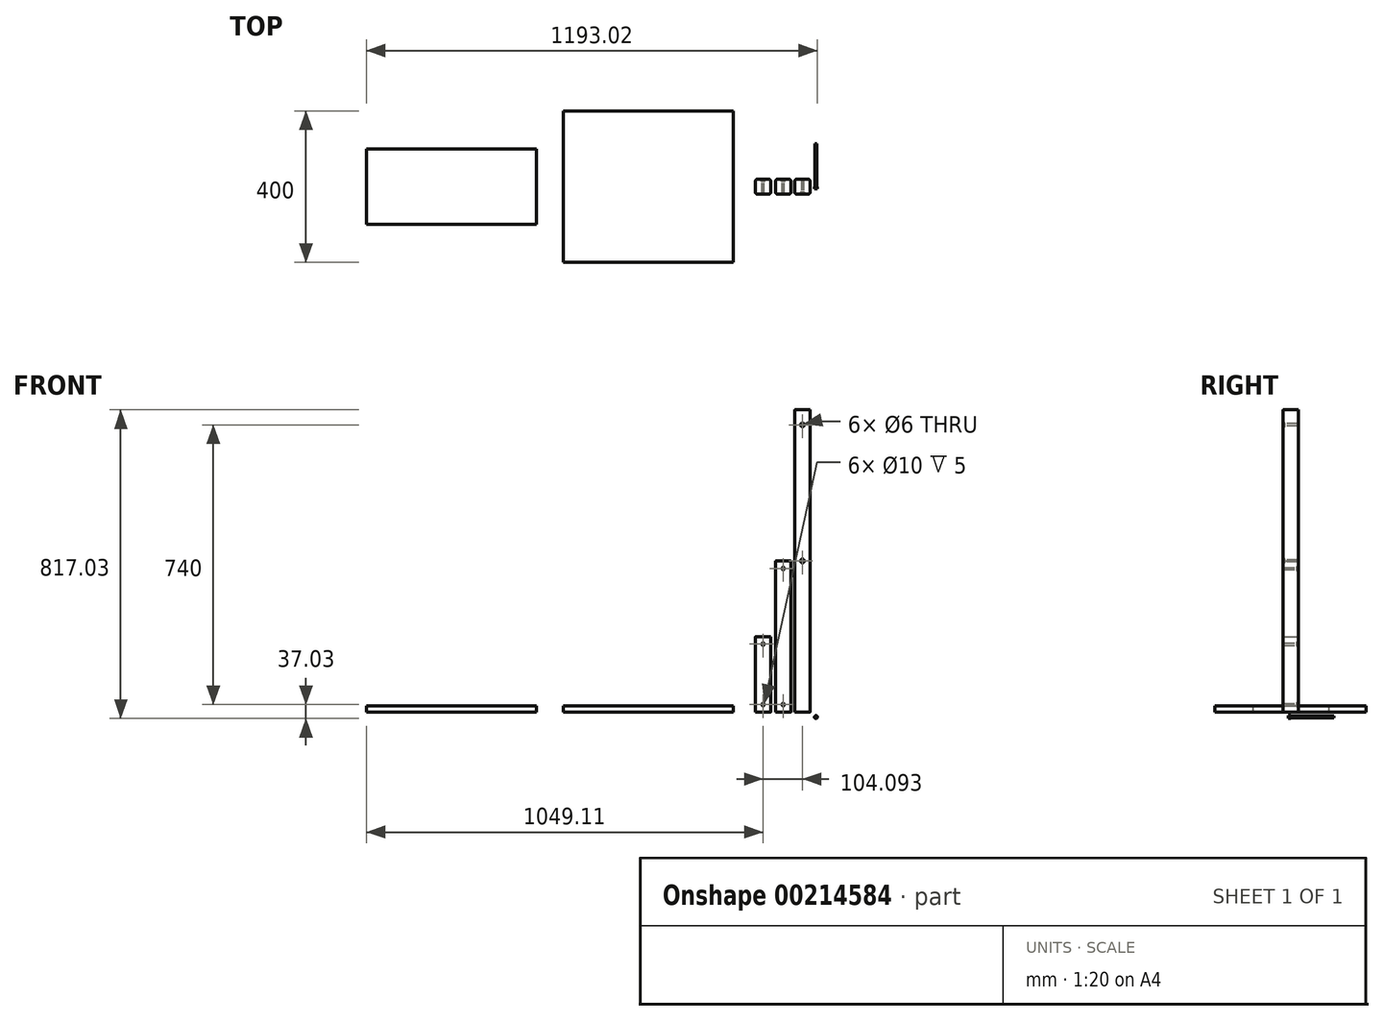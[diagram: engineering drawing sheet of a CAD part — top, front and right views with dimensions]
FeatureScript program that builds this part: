
annotation { "Feature Type Name" : "Feature", "Feature Type Description" : "" }
export const myFeature = defineFeature(function(context is Context, id is Id, definition is map)
    precondition{}
    {
        {
            var Q0;
            Q0=qCreatedBy(makeId("Top.planeOp"),FACE);
            var sketch = newSketch(context, id + "F0", { "sketchPlane" : qUnion([Q0])});
            skLineSegment(sketch, "E0.bottom", {"start": v(20, -20) * mm, "end": v(-20, -20) * mm});
            skLineSegment(sketch, "E0.top", {"start": v(20, 20) * mm, "end": v(-20, 20) * mm});
            skLineSegment(sketch, "E0.left", {"start": v(20, -20) * mm, "end": v(20, 20) * mm});
            skLineSegment(sketch, "E0.right", {"start": v(-20, -20) * mm, "end": v(-20, 20) * mm});
            skPoint(sketch, "E0.middle", {"position": v(0, 0) * mm});
            skSolve(sketch);
        }
        {
            var Q0;
            Q0 = qSketchRegion(id + "F0", true);
            extrude(context, id + "F1", {"entities" : qUnion([Q0]), "depth" : 800 * mm});
        }
        {
            var Q0;
            Q0=makeQuery(id+"F1.opExtrude","SWEPT_FACE",FACE,{"disambiguationData":[OSD([sQuery(id+"F0.wireOp",EDGE,"E0.bottom")])]});
            var sketch = newSketch(context, id + "F2", { "sketchPlane" : qUnion([Q0])});
            skPoint(sketch, "E1", {"position": v(0, 400) * mm});
            skPoint(sketch, "E2", {"position": v(0, 760) * mm});
            skSolve(sketch);
        }
        {
            var Q0;
            Q0=sQuery(id+"F2.wireOp",VERTEX,"E2");
            var Q1;
            Q1=sQuery(id+"F2.wireOp",VERTEX,"E1");
            var Q2;
            Q2=makeQuery(id+"F1.opExtrude","SWEPT_BODY",BODY,{"disambiguationData":[OSD([sQuery(id+"F0.wireOp",EDGE,"E0.bottom"),sQuery(id+"F0.wireOp",EDGE,"E0.top"),sQuery(id+"F0.wireOp",EDGE,"E0.left"),sQuery(id+"F0.wireOp",EDGE,"E0.right")])]});
            hole(context, id + "F3", {"style" : HoleStyle.C_BORE, "endStyle" : HoleEndStyle.THROUGH, "holeDiameter" : 6 * mm, "cBoreDiameter" : 10 * mm, "cBoreDepth" : 5 * mm, "locations" : qUnion([Q0, Q1]), "scope" : qUnion([Q2]), "isTappedThrough" : true});
        }
        {
            var Q0;
            Q0=makeQuery(id+"F1.opExtrude","SWEPT_EDGE",EDGE,{"disambiguationData":[OSD([sQuery(id+"F0.wireOp",EDGE,"E0.top"),sQuery(id+"F0.wireOp",EDGE,"E0.right")])]});
            var Q1;
            Q1=makeQuery(id+"F1.opExtrude","SWEPT_EDGE",EDGE,{"disambiguationData":[OSD([sQuery(id+"F0.wireOp",EDGE,"E0.top"),sQuery(id+"F0.wireOp",EDGE,"E0.left")])]});
            var Q2;
            Q2=makeQuery(id+"F1.opExtrude","SWEPT_EDGE",EDGE,{"disambiguationData":[OSD([sQuery(id+"F0.wireOp",EDGE,"E0.bottom"),sQuery(id+"F0.wireOp",EDGE,"E0.right")])]});
            var Q3;
            Q3=makeQuery(id+"F1.opExtrude","SWEPT_EDGE",EDGE,{"disambiguationData":[OSD([sQuery(id+"F0.wireOp",EDGE,"E0.bottom"),sQuery(id+"F0.wireOp",EDGE,"E0.left")])]});
            fillet(context, id + "F4", {"entities" : qUnion([Q0, Q1, Q2, Q3]), "radius" : 5 * mm, "tangentPropagation" : true, "allowEdgeOverflow" : false});
        }
        {
            var Q0;
            Q0=qCreatedBy(makeId("Front.planeOp"),FACE);
            var sketch = newSketch(context, id + "F5", { "sketchPlane" : qUnion([Q0])});
            skCircle(sketch, "E3", {"center": v(35.82, -13.03) * mm, "radius": 4 * mm});
            skSolve(sketch);
        }
        {
            var Q0;
            Q0 = qSketchRegion(id + "F5", true);
            extrude(context, id + "F6", {"entities" : qUnion([Q0]), "depth" : 6 * mm});
        }
        {
            var Q0;
            Q0=makeQuery(id+"F6.opExtrude","CAP_FACE",FACE,{"disambiguationData":[OSD([sQuery(id+"F5.wireOp",EDGE,"E3")])],"isStart":false});
            var sketch = newSketch(context, id + "F7", { "sketchPlane" : qUnion([Q0])});
            skCircle(sketch, "E4", {"center": v(35.82, -13.03) * mm, "radius": 2.5 * mm});
            skSolve(sketch);
        }
        {
            var Q0;
            Q0 = qSketchRegion(id + "F7", true);
            extrude(context, id + "F8", {"entities" : qUnion([Q0]), "operationType" : NewBodyOperationType.ADD, "oppositeDirection" : true, "depth" : 120 * mm});
        }
        {
            var Q0;
            Q0=makeQuery(id+"F6.opExtrude","CAP_FACE",FACE,{"disambiguationData":[OSD([sQuery(id+"F5.wireOp",EDGE,"E3")])],"isStart":false});
            var sketch = newSketch(context, id + "F9", { "sketchPlane" : qUnion([Q0])});
            skCircle(sketch, "E5", {"center": v(35.82, -13.03) * mm, "radius": 2.5 * mm});
            skCircle(sketch, "E6.cCircle", {"center": v(35.82, -13.03) * mm, "radius": 2.5 * mm, "construction": true});
            skLineSegment(sketch, "E6.0", {"start": v(36.75, -10.3) * mm, "end": v(38.66, -12.46) * mm});
            skLineSegment(sketch, "E6.1", {"start": v(38.66, -12.46) * mm, "end": v(37.73, -15.2) * mm});
            skLineSegment(sketch, "E6.2", {"start": v(37.73, -15.2) * mm, "end": v(34.9, -15.76) * mm});
            skLineSegment(sketch, "E6.3", {"start": v(34.9, -15.76) * mm, "end": v(33, -13.59) * mm});
            skLineSegment(sketch, "E6.4", {"start": v(33, -13.59) * mm, "end": v(33.92, -10.85) * mm});
            skLineSegment(sketch, "E6.5", {"start": v(33.92, -10.85) * mm, "end": v(36.75, -10.3) * mm});
            skPoint(sketch, "E6.0.midPoint", {"position": v(37.7, -11.38) * mm});
            skSolve(sketch);
        }
        {
            var Q0;
            Q0 = qSketchRegion(id + "F9", true);
            var Q1;
            Q1=sQuery(id+"F9.wireOp",EDGE,"E6.0");
            var Q2;
            Q2=sQuery(id+"F9.wireOp",EDGE,"E6.5");
            var Q3;
            Q3=sQuery(id+"F9.wireOp",EDGE,"E6.4");
            var Q4;
            Q4=sQuery(id+"F9.wireOp",EDGE,"E6.3");
            var Q5;
            Q5=sQuery(id+"F9.wireOp",EDGE,"E6.1");
            var Q6;
            Q6=sQuery(id+"F9.wireOp",EDGE,"E6.2");
            extrude(context, id + "F10", {"entities" : qUnion([Q0]), "operationType" : NewBodyOperationType.REMOVE, "surfaceEntities" : qUnion([Q1, Q2, Q3, Q4, Q5, Q6]), "oppositeDirection" : true, "depth" : 4 * mm});
        }
        {
            var Q0;
            Q0=qCreatedBy(makeId("Top.planeOp"),FACE);
            var sketch = newSketch(context, id + "F11", { "sketchPlane" : qUnion([Q0])});
            skLineSegment(sketch, "E7.bottom", {"start": v(-30.83, -20) * mm, "end": v(-70.83, -20) * mm});
            skLineSegment(sketch, "E7.top", {"start": v(-30.83, 20) * mm, "end": v(-70.83, 20) * mm});
            skLineSegment(sketch, "E7.left", {"start": v(-30.83, -20) * mm, "end": v(-30.83, 20) * mm});
            skLineSegment(sketch, "E7.right", {"start": v(-70.83, -20) * mm, "end": v(-70.83, 20) * mm});
            skPoint(sketch, "E7.middle", {"position": v(-50.83, 0) * mm});
            skSolve(sketch);
        }
        {
            var Q0;
            Q0 = qSketchRegion(id + "F11", true);
            extrude(context, id + "F12", {"entities" : qUnion([Q0]), "depth" : 400 * mm});
        }
        {
            var Q0;
            Q0=makeQuery(id+"F12.opExtrude","SWEPT_EDGE",EDGE,{"disambiguationData":[OSD([sQuery(id+"F11.wireOp",EDGE,"E7.bottom"),sQuery(id+"F11.wireOp",EDGE,"E7.right")])]});
            var Q1;
            Q1=makeQuery(id+"F12.opExtrude","SWEPT_EDGE",EDGE,{"disambiguationData":[OSD([sQuery(id+"F11.wireOp",EDGE,"E7.bottom"),sQuery(id+"F11.wireOp",EDGE,"E7.left")])]});
            var Q2;
            Q2=makeQuery(id+"F12.opExtrude","SWEPT_EDGE",EDGE,{"disambiguationData":[OSD([sQuery(id+"F11.wireOp",EDGE,"E7.top"),sQuery(id+"F11.wireOp",EDGE,"E7.left")])]});
            var Q3;
            Q3=makeQuery(id+"F12.opExtrude","SWEPT_EDGE",EDGE,{"disambiguationData":[OSD([sQuery(id+"F11.wireOp",EDGE,"E7.top"),sQuery(id+"F11.wireOp",EDGE,"E7.right")])]});
            fillet(context, id + "F13", {"entities" : qUnion([Q0, Q1, Q2, Q3]), "radius" : 5 * mm, "tangentPropagation" : true, "allowEdgeOverflow" : false});
        }
        {
            var Q0;
            Q0=makeQuery(id+"F12.opExtrude","SWEPT_FACE",FACE,{"disambiguationData":[OSD([sQuery(id+"F11.wireOp",EDGE,"E7.top")])]});
            var sketch = newSketch(context, id + "F14", { "sketchPlane" : qUnion([Q0])});
            skPoint(sketch, "E8", {"position": v(50.83, 20) * mm});
            skPoint(sketch, "E8.positionSnap0", {"position": v(50.83, 0) * mm});
            skPoint(sketch, "E9", {"position": v(50.83, 380) * mm});
            skSolve(sketch);
        }
        {
            var Q0;
            Q0=sQuery(id+"F14.wireOp",VERTEX,"E8");
            var Q1;
            Q1=sQuery(id+"F14.wireOp",VERTEX,"E9");
            var Q2;
            Q2=makeQuery(id+"F12.opExtrude","SWEPT_BODY",BODY,{"disambiguationData":[OSD([sQuery(id+"F11.wireOp",EDGE,"E7.bottom"),sQuery(id+"F11.wireOp",EDGE,"E7.top"),sQuery(id+"F11.wireOp",EDGE,"E7.left"),sQuery(id+"F11.wireOp",EDGE,"E7.right")])]});
            hole(context, id + "F15", {"style" : HoleStyle.C_BORE, "endStyle" : HoleEndStyle.THROUGH, "holeDiameter" : 6 * mm, "cBoreDiameter" : 10 * mm, "cBoreDepth" : 5 * mm, "locations" : qUnion([Q0, Q1]), "scope" : qUnion([Q2]), "isTappedThrough" : true});
        }
        {
            var Q0;
            Q0=qCreatedBy(makeId("Top.planeOp"),FACE);
            var sketch = newSketch(context, id + "F16", { "sketchPlane" : qUnion([Q0])});
            skLineSegment(sketch, "E10.bottom", {"start": v(-84.1, -20) * mm, "end": v(-124.1, -20) * mm});
            skLineSegment(sketch, "E10.top", {"start": v(-84.1, 20) * mm, "end": v(-124.1, 20) * mm});
            skLineSegment(sketch, "E10.left", {"start": v(-84.1, -20) * mm, "end": v(-84.1, 20) * mm});
            skLineSegment(sketch, "E10.right", {"start": v(-124.1, -20) * mm, "end": v(-124.1, 20) * mm});
            skPoint(sketch, "E10.middle", {"position": v(-104.1, 0) * mm});
            skSolve(sketch);
        }
        {
            var Q0;
            Q0 = qSketchRegion(id + "F16", true);
            extrude(context, id + "F17", {"entities" : qUnion([Q0]), "depth" : 200 * mm});
        }
        {
            var Q0;
            Q0=makeQuery(id+"F17.opExtrude","SWEPT_EDGE",EDGE,{"disambiguationData":[OSD([sQuery(id+"F16.wireOp",EDGE,"E10.top"),sQuery(id+"F16.wireOp",EDGE,"E10.right")])]});
            var Q1;
            Q1=makeQuery(id+"F17.opExtrude","SWEPT_EDGE",EDGE,{"disambiguationData":[OSD([sQuery(id+"F16.wireOp",EDGE,"E10.top"),sQuery(id+"F16.wireOp",EDGE,"E10.left")])]});
            var Q2;
            Q2=makeQuery(id+"F17.opExtrude","SWEPT_EDGE",EDGE,{"disambiguationData":[OSD([sQuery(id+"F16.wireOp",EDGE,"E10.bottom"),sQuery(id+"F16.wireOp",EDGE,"E10.right")])]});
            var Q3;
            Q3=makeQuery(id+"F17.opExtrude","SWEPT_EDGE",EDGE,{"disambiguationData":[OSD([sQuery(id+"F16.wireOp",EDGE,"E10.bottom"),sQuery(id+"F16.wireOp",EDGE,"E10.left")])]});
            fillet(context, id + "F18", {"entities" : qUnion([Q0, Q1, Q2, Q3]), "radius" : 5 * mm, "tangentPropagation" : true, "allowEdgeOverflow" : false});
        }
        {
            var Q0;
            Q0=makeQuery(id+"F17.opExtrude","SWEPT_FACE",FACE,{"disambiguationData":[OSD([sQuery(id+"F16.wireOp",EDGE,"E10.top")])]});
            var sketch = newSketch(context, id + "F19", { "sketchPlane" : qUnion([Q0])});
            skPoint(sketch, "E11", {"position": v(104.1, 20) * mm});
            skPoint(sketch, "E11.positionSnap0", {"position": v(104.1, 0) * mm});
            skPoint(sketch, "E12", {"position": v(104.1, 200) * mm});
            skPoint(sketch, "E13", {"position": v(104.1, 180) * mm});
            skSolve(sketch);
        }
        {
            var Q0;
            Q0=sQuery(id+"F19.wireOp",VERTEX,"E11");
            var Q1;
            Q1=sQuery(id+"F19.wireOp",VERTEX,"E13");
            var Q2;
            Q2=makeQuery(id+"F17.opExtrude","SWEPT_BODY",BODY,{"disambiguationData":[OSD([sQuery(id+"F16.wireOp",EDGE,"E10.bottom"),sQuery(id+"F16.wireOp",EDGE,"E10.top"),sQuery(id+"F16.wireOp",EDGE,"E10.left"),sQuery(id+"F16.wireOp",EDGE,"E10.right")])]});
            hole(context, id + "F20", {"style" : HoleStyle.C_BORE, "endStyle" : HoleEndStyle.THROUGH, "holeDiameter" : 6 * mm, "cBoreDiameter" : 10 * mm, "cBoreDepth" : 5 * mm, "locations" : qUnion([Q0, Q1]), "scope" : qUnion([Q2]), "isTappedThrough" : true});
        }
        {
            var Q0;
            Q0=qCreatedBy(makeId("Top.planeOp"),FACE);
            var sketch = newSketch(context, id + "F21", { "sketchPlane" : qUnion([Q0])});
            skLineSegment(sketch, "E14.bottom", {"start": v(-182.57, 200) * mm, "end": v(-632.57, 200) * mm});
            skLineSegment(sketch, "E14.top", {"start": v(-182.57, -200) * mm, "end": v(-632.57, -200) * mm});
            skLineSegment(sketch, "E14.left", {"start": v(-182.57, 200) * mm, "end": v(-182.57, -200) * mm});
            skLineSegment(sketch, "E14.right", {"start": v(-632.57, 200) * mm, "end": v(-632.57, -200) * mm});
            skPoint(sketch, "E14.middle", {"position": v(-407.57, 0) * mm});
            skSolve(sketch);
        }
        {
            var Q0;
            Q0 = qSketchRegion(id + "F21", true);
            extrude(context, id + "F22", {"entities" : qUnion([Q0]), "depth" : 16 * mm});
        }
        {
            var Q0;
            Q0=qCreatedBy(makeId("Top.planeOp"),FACE);
            var sketch = newSketch(context, id + "F23", { "sketchPlane" : qUnion([Q0])});
            skLineSegment(sketch, "E15.bottom", {"start": v(-703.2, -100) * mm, "end": v(-1153.2, -100) * mm});
            skLineSegment(sketch, "E15.top", {"start": v(-703.2, 100) * mm, "end": v(-1153.2, 100) * mm});
            skLineSegment(sketch, "E15.left", {"start": v(-703.2, -100) * mm, "end": v(-703.2, 100) * mm});
            skLineSegment(sketch, "E15.right", {"start": v(-1153.2, -100) * mm, "end": v(-1153.2, 100) * mm});
            skPoint(sketch, "E15.middle", {"position": v(-928.2, 0) * mm});
            skSolve(sketch);
        }
        {
            var Q0;
            Q0=makeQuery(id+"F23.imprint","IMPRINT",FACE,{"disambiguationData":[TD([[makeQuery(id+"F23.imprint","IMPRINT",EDGE,{"derivedFrom":sQuery(id+"F23.wireOp",EDGE,"E15.bottom")}),-1.0]])]});
            extrude(context, id + "F24", {"entities" : qUnion([Q0]), "depth" : 16 * mm});
        }
    });
